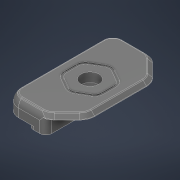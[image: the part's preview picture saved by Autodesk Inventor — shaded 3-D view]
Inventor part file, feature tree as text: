
AUTODESK INVENTOR PART (.ipt)
format: ipt  version: 2022.1 (Build 261234000, 234)  size: 942,080 bytes
history: native  units: mm
features: projected_geometry x17, extrude x15, sketch x15, direct_edit x10, move_body x10, chamfer x8, fillet x7, delete_face x5, other x1
ambient origin geometry x8: Origin, YZ Plane, XZ Plane, XY Plane, X Axis, Y Axis, Z Axis, Center Point
bodies: Volumenkörper1 (feature_tree)
feature tree (88):
  extrude  "Extrusion1"  Depth=10.0mm TaperAngle=0.0deg
  extrude  "Extrusion2"  Depth=10.0mm
  extrude  "Extrusion3"  Depth=1.0mm
  fillet  "Rundung1"  Radius=5.8mm
  fillet  "Rundung2"  Radius=1.0mm
  extrude  "Extrusion4"  Depth=1.0mm
  chamfer  "Fase1"  Distance=1.2mm
  direct_edit  "Direktbearbeitung1"
  extrude  "Extrusion5"  TaperAngle=0.0deg  [1 undecoded]
  chamfer  "Fase2"  Distance=0.8mm
  extrude  "Extrusion6"  Depth=4.0mm
  chamfer  "Fase3"  Distance=0.8mm
  chamfer  "Fase4"  Distance=0.4mm Angle=45.0deg
  delete_face  "Fläche löschen1"
  delete_face  "Fläche löschen2"
  delete_face  "Fläche löschen3"
  delete_face  "Fläche löschen4"
  direct_edit  "Direktbearbeitung2"
  extrude  "Extrusion7"  TaperAngle=0.0deg  [1 undecoded]
  fillet  "Rundung7"  Radius=0.8mm
  direct_edit  "Direktbearbeitung3"
  direct_edit  "Direktbearbeitung4"
  extrude  "Extrusion8"  Depth=0.4mm TaperAngle=0.0deg
  direct_edit  "Direktbearbeitung5"
  chamfer  "Fase9"  [1 undecoded]
  fillet  "Rundung8"  Radius=0.2mm
  extrude  "Extrusion9"  Depth=0.4mm TaperAngle=0.0deg
  extrude  "Extrusion10"  Depth=1.2mm TaperAngle=45.0deg
  extrude  "Extrusion11"  Depth=3.0mm
  extrude  "Extrusion12"  Depth=0.4mm TaperAngle=0.0deg
  chamfer  "Fase10"  Distance=0.4mm
  direct_edit  "Direktbearbeitung6"
  extrude  "Extrusion13"  Depth=10.0mm TaperAngle=0.0deg
  fillet  "Rundung9"  Radius=5.8mm
  fillet  "Rundung10"  Radius=6.0mm
  direct_edit  "Direktbearbeitung7"
  delete_face  "Fläche löschen5"
  direct_edit  "Direktbearbeitung8"
  direct_edit  "Direktbearbeitung9"
  chamfer  "Fase11"  Distance=0.2mm
  direct_edit  "Direktbearbeitung10"
  extrude  "Extrusion14"  Depth=10.0mm TaperAngle=45.0deg
  fillet  "Rundung11"  [1 undecoded]
  chamfer  "Fase12"  Distance=6.0mm
  extrude  "Extrusion15"  Depth=10.0mm
  sketch  "Skizze1"  dims[d0=7.7mm d1=10.0mm d2=0.0mm]
  projected_geometry  "Projizierte Kontur1"
  sketch  "Skizze2"  dims[d3=10.0mm d4=0.0mm d5=35.0mm]
  projected_geometry  "Projizierte Kontur2"
  sketch  "Skizze3"  dims[d6=5.8mm d7=1.0mm d8=5.8mm d9=1.0mm d10=0.0mm]
  sketch  "Skizze4"  dims[d11=2.0mm d12=1.0mm]
  sketch  "Skizze5"  dims[d13=11.0mm]
  projected_geometry  "Projizierte Kontur3"
  sketch  "Skizze6"  dims[d14=0.8mm]
  projected_geometry  "Projizierte Kontur4"
  sketch  "Skizze7"  dims[d15=2.0mm]
  projected_geometry  "Projizierte Kontur5"
  projected_geometry  "Projizierte Kontur6"
  sketch  "Skizze8"  dims[d16=2.8mm d17=1.2mm d18=0.0mm]
  projected_geometry  "Projizierte Kontur7"
  projected_geometry  "Projizierte Kontur8"
  sketch  "Skizze9"  dims[d19=0.4mm d20=2.0mm d21=45.0deg d22=0.0mm d23=0.0mm d24=-0.4mm]
  projected_geometry  "Projizierte Kontur9"
  sketch  "Skizze10"  dims[d25=5.6mm]
  projected_geometry  "Projizierte Kontur10"
  projected_geometry  "Projizierte Kontur11"
  projected_geometry  "Projizierte Kontur12"
  projected_geometry  "Projizierte Kontur13"
  sketch  "Skizze11"  dims[d26=5.6mm d27=0.8mm d28=0.0mm]
  projected_geometry  "Projizierte Kontur14"
  sketch  "Skizze12"  dims[d29=0.4mm d30=2.0mm d31=45.0deg d32=4.0mm]
  projected_geometry  "Projizierte Kontur15"
  sketch  "Skizze13"  dims[d33=4.0mm d34=0.8mm d35=0.0mm d36=0.4mm d37=2.0mm d38=45.0deg]
  sketch  "Skizze14"  dims[d39=0.4mm d40=2.0mm d41=45.0deg d42=0.0mm d43=0.0mm d44=-1.0mm d45=0.8mm d46=0.0mm]
  projected_geometry  "Projizierte Kontur16"
  sketch  "Skizze15"  dims[d63=4.0mm d64=0.0mm d65=0.0mm d66=0.4mm d67=0.0mm d68=0.0mm d69=-0.8mm d70=0.2mm d71=0.0mm d72=0.0mm d73=0.0mm d74=0.4mm d75=1.2mm d76=2.0mm d77=45.0deg d78=3.0mm d79=0.4mm d80=0.0mm d81=0.4mm d82=0.0mm d83=0.2mm d84=0.0mm d85=5.8mm d86=6.0mm d87=0.2mm d88=0.0mm d89=0.2mm d90=2.0mm d91=45.0deg d92=0.0mm d93=0.0mm d94=-1.0mm d95=6.0mm d96=0.5mm d97=6.0mm d98=1.0mm d99=0.0mm d100=2.0mm d101=0.8mm d102=0.0mm d103=0.0mm d104=0.1mm d105=0.0mm d106=0.0mm d107=0.4mm d108=0.0mm d109=0.0mm d110=0.2mm d111=0.2mm d112=2.0mm d113=45.0deg d114=0.0mm d115=0.0mm d116=0.4mm d117=10.0mm d118=0.0mm d119=2.4mm d120=0.4mm d121=2.0mm d122=45.0deg d123=0.8mm d124=0.8mm d125=2.2mm d126=3.0mm d127=10.0mm d128=0.0mm]
  projected_geometry  "Projizierte Kontur17"
  other  "midspan_panel_clip_4mm_x7"
  move_body  "Verschieben1"
  move_body  "Verschieben2"
  move_body  "Verschieben3"
  move_body  "Verschieben4"
  move_body  "Verschieben5"
  move_body  "Verschieben6"
  move_body  "Verschieben7"
  move_body  "Verschieben8"
  move_body  "Verschieben9"
  move_body  "Verschieben10"
note: 4 required parameter values undecoded (feature->parameter linkage not recoverable at this tier; creation-order binding heuristic only, values carry confidence <= 0.55)
